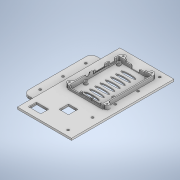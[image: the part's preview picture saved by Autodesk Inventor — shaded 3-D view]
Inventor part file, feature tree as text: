
AUTODESK INVENTOR PART (.ipt)
format: ipt  version: 2022 (Build 260153000, 153)  size: 488,448 bytes
history: native  units: mm
features: reference x13, extrude x10, sketch x10, other x8, fillet x3, projected_geometry x1, imported_body x1
ambient origin geometry x8: Origin, YZ Plane, XZ Plane, XY Plane, X Axis, Y Axis, Z Axis, Center Point
bodies: Body1 (feature_tree)
feature tree (46):
  other  "Твердое тело1"
  extrude  "Выдавливание1"  Depth=10.0mm
  extrude  "Выдавливание2"  Depth=10.0mm
  extrude  "Выдавливание3"  Depth=10.0mm
  extrude  "Выдавливание4"  Depth=13.0mm
  extrude  "Выдавливание5"  Depth=3.5mm TaperAngle=0.0deg
  extrude  "Выдавливание6"  Depth=11.0mm
  extrude  "Выдавливание7"  Depth=11.0mm
  fillet  "Сопряжение1"  Radius=3.5mm
  fillet  "Сопряжение2"  Radius=120.0mm
  extrude  "Выдавливание8"  Depth=30.0mm
  extrude  "Выдавливание9"  Depth=30.0mm
  fillet  "Сопряжение3"  Radius=3.5mm
  extrude  "Выдавливание10"  Depth=30.0mm
  sketch  "Эскиз1"
  projected_geometry  "Спроецированная петля1"
  sketch  "Эскиз2"
  reference  "Ссылка1"
  sketch  "Эскиз3"
  sketch  "Эскиз4"
  sketch  "Эскиз5"
  sketch  "Эскиз6"
  sketch  "Эскиз7"
  reference  "Ссылка2"
  reference  "Ссылка3"
  reference  "Ссылка4"
  reference  "Ссылка5"
  reference  "Ссылка6"
  reference  "Ссылка7"
  reference  "Ссылка8"
  sketch  "Эскиз8"
  reference  "Ссылка9"
  reference  "Ссылка10"
  reference  "Ссылка11"
  reference  "Ссылка12"
  reference  "Ссылка13"
  sketch  "Эскиз9"
  sketch  "Эскиз10"
  imported_body  "БазТело1"
  other  "<path> - Robot.iam"
  other  "000.000 - Robot.iam"
  other  "000.002 - bamper:1"
  other  "000.001 - Bottom:1"
  other  "000.002 - bamper:2"
  other  "01_Крепление_мотора:1"
  other  "01_Крепление_мотора:3"
note: 1 file-system path scrubbed to <path> (originals preserved in map.json)
